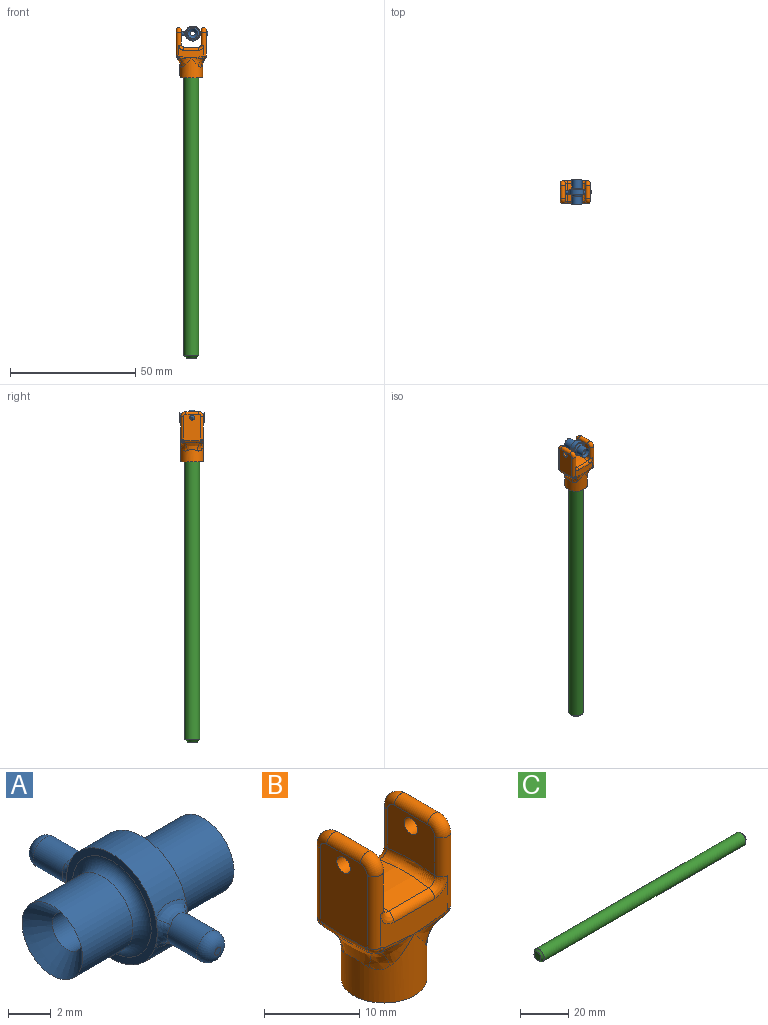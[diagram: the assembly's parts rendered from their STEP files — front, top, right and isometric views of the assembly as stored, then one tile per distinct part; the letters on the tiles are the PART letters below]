
ASSEMBLY  parts=3 mates=1
PART A: 27 faces, bbox 10.1x12.1x6.6 mm
  f0: cylinder r=3mm len=5.74mm, axis (1,0,0), area 14.3mm2, adj f4,f5,f14,f18
  f1: cylinder r=1mm len=2.93mm, axis (1,0,0), area 18.4mm2, adj f8,f25
  f2: cylinder r=3mm len=5.81mm, axis (1,0,0), area 14.8mm2, adj f4,f5,f15,f19
  f3: cylinder r=2mm len=4mm, axis (1,0,0), area 43.6mm2, adj f7,f23
  f4: plane 6.08x6.08mm, normal (1,0,0), area 7mm2, adj f0,f2,f16,f17,f23
  f5: plane 6.08x6.08mm, normal (-1,0,0), area 7mm2, adj f0,f2,f13,f20,f24
  f6: cylinder r=2mm len=4mm, axis (1,0,0), area 41.9mm2, adj f8,f24
  f7: cone r=1mm half-angle=45deg, axis (1,0,0), area 13.1mm2, adj f3,f26
  f8: cone r=2mm half-angle=45deg, axis (-1,0,0), area 13.3mm2, adj f1,f6
  f9: plane 0.4x0.4mm, normal (0,1,0), area 0.1mm2, adj f21
  f10: cylinder r=0.8mm len=2.11mm, axis (0,1,0), area 10mm2, adj f17,f18,f19,f20,f21
  f11: plane 0.4x0.4mm, normal (0,-1,0), area 0.1mm2, adj f22
  f12: cylinder r=0.8mm len=2.11mm, axis (0,1,0), area 10mm2, adj f13,f14,f15,f16,f22
  f13: bspline ~1.77x0.65mm, area 0.8mm2, adj f5,f12,f14,f15
  f14: bspline ~2.33x0.81mm, area 1.2mm2, adj f0,f12,f13,f16
  f15: bspline ~2x0.7mm, area 1.3mm2, adj f2,f12,f13,f16
  f16: bspline ~1.78x0.67mm, area 0.8mm2, adj f4,f12,f14,f15
  f17: bspline ~1.77x0.65mm, area 0.8mm2, adj f4,f10,f18,f19
  f18: bspline ~2.33x0.81mm, area 1.2mm2, adj f0,f10,f17,f20
  f19: bspline ~2x0.7mm, area 1.3mm2, adj f2,f10,f17,f20
  f20: bspline ~1.78x0.67mm, area 0.8mm2, adj f5,f10,f18,f19
  f21: torus R=0.2mm, axis (0,-1,0), area 3.4mm2, adj f9,f10
  f22: torus R=0.2mm, axis (0,-1,0), area 3.4mm2, adj f11,f12
  f23: torus R=2.6mm, axis (1,0,0), area 13.1mm2, adj f3,f4
  f24: torus R=2.6mm, axis (1,0,0), area 13.1mm2, adj f5,f6
  f25: plane 2.04x2.04mm, normal (1,0,0), area 0.1mm2, adj f1,f26
  f26: cylinder r=1.02mm len=5.09mm, axis (-1,0,0), area 32.7mm2, adj f7,f25
PART B: 63 faces, bbox 12.4x9.7x20.5 mm
  f0: plane 10.37x5.36mm, normal (0,1,0), area 29.1mm2, adj f12,f14,f38,f39,f40,f41,f42,f43
  f1: plane 10.33x5.33mm, normal (0,-1,0), area 29.1mm2, adj f8,f13,f30,f31,f32,f49,f50,f51
  f2: plane 7x6mm, normal (-1,0,0), area 37.2mm2, adj f8,f9,f10,f11,f12,f28,f54
  f3: cylinder r=4.5mm len=9mm, axis (0,0,-1), area 148.7mm2, adj f18,f19,f20,f21,f22,f23,f24,f25
  f4: plane 7x6mm, normal (1,0,0), area 37.2mm2, adj f13,f14,f15,f16,f17,f29,f57
  f5: plane 10.55x7mm, normal (-1,0,0), area 69.9mm2, adj f13,f14,f15,f16,f17,f29,f34,f35
  f6: plane 10.55x7mm, normal (1,0,0), area 69.9mm2, adj f8,f9,f10,f11,f12,f28,f45,f46
  f7: cylinder r=21.21mm len=7.35mm, axis (-1,0,0), area 44.3mm2, adj f53,f54,f57,f58
  f8: cylinder r=1mm len=9.36mm, axis (0,0,1), area 22.6mm2, adj f1,f2,f6,f9,f48,f56
  f9: torus R=1mm, axis (-1,0,0), area 8.1mm2, adj f2,f6,f8,f10
  f10: cylinder r=1mm len=5mm, axis (0,-1,0), area 15.7mm2, adj f2,f6,f9,f11
  f11: torus R=1mm, axis (-1,0,0), area 8.1mm2, adj f2,f6,f10,f12
  f12: cylinder r=1mm len=9.36mm, axis (0,0,-1), area 22.6mm2, adj f0,f2,f6,f11,f44,f52
  f13: cylinder r=1mm len=9.36mm, axis (0,0,-1), area 22.6mm2, adj f1,f4,f5,f15,f33,f59
  f14: cylinder r=1mm len=9.36mm, axis (0,0,1), area 22.6mm2, adj f0,f4,f5,f16,f37,f55
  f15: torus R=1mm, axis (-1,0,0), area 8.1mm2, adj f4,f5,f13,f17
  f16: torus R=1mm, axis (-1,0,0), area 8.1mm2, adj f4,f5,f14,f17
  f17: cylinder r=1mm len=5mm, axis (0,1,0), area 15.7mm2, adj f4,f5,f15,f16
  f18: bspline ~5.51x3.49mm, area 4.6mm2, adj f3,f19,f41
  f19: bspline ~3.75x3.7mm, area 6.7mm2, adj f3,f18,f20,f42,f43,f45
  f20: bspline ~8.76x3.84mm, area 17mm2, adj f3,f19,f21,f46
  f21: bspline ~3.75x3.6mm, area 6.7mm2, adj f3,f20,f22,f47,f49,f50
  f22: bspline ~5.51x3.49mm, area 4.6mm2, adj f3,f21,f51
  f23: bspline ~5.51x3.49mm, area 4.6mm2, adj f3,f24,f30
  f24: bspline ~3.75x3.7mm, area 6.7mm2, adj f3,f23,f25,f31,f32,f34
  f25: bspline ~8.76x3.84mm, area 17mm2, adj f3,f24,f26,f35
  f26: bspline ~3.75x3.6mm, area 6.7mm2, adj f3,f25,f27,f36,f38,f39
  f27: bspline ~5.51x3.49mm, area 4.6mm2, adj f3,f26,f40
  f28: cylinder r=1mm len=2mm, axis (1,0,0), area 12.6mm2, adj f2,f6
  f29: cylinder r=1mm len=2mm, axis (1,0,0), area 12.6mm2, adj f4,f5
  f30: bspline ~4.78x0.76mm, area 1.2mm2, adj f1,f23,f31
  f31: bspline ~0.8x0.45mm, area 0.1mm2, adj f1,f24,f30,f32
  f32: bspline ~1.15x1.11mm, area 0.7mm2, adj f1,f24,f31,f33
  f33: sphere r=1mm, area 1.1mm2, adj f13,f32,f34
  f34: bspline ~0.98x0.87mm, area 0.5mm2, adj f5,f24,f33,f35
  f35: bspline ~6.85x0.85mm, area 5.5mm2, adj f5,f25,f34,f36
  f36: bspline ~0.97x0.85mm, area 0.5mm2, adj f5,f26,f35,f37
  f37: sphere r=1mm, area 1.1mm2, adj f14,f36,f38
  f38: bspline ~1.2x1.14mm, area 0.7mm2, adj f0,f26,f37,f39
  f39: bspline ~0.79x0.44mm, area 0.1mm2, adj f0,f26,f38,f40
  f40: bspline ~4.9x0.78mm, area 1.2mm2, adj f0,f27,f39
  f41: bspline ~4.69x0.74mm, area 1.2mm2, adj f0,f18,f42
  f42: bspline ~0.8x0.45mm, area 0.1mm2, adj f0,f19,f41,f43
  f43: bspline ~1.31x1.18mm, area 0.7mm2, adj f0,f19,f42,f44
  f44: sphere r=1mm, area 1mm2, adj f12,f43,f45
  f45: bspline ~0.98x0.85mm, area 0.5mm2, adj f6,f19,f44,f46
  f46: bspline ~7.61x0.93mm, area 5.5mm2, adj f6,f20,f45,f47
  f47: bspline ~0.98x0.85mm, area 0.5mm2, adj f6,f21,f46,f48
  f48: sphere r=1mm, area 1mm2, adj f8,f47,f49
  f49: bspline ~1.2x1.14mm, area 0.7mm2, adj f1,f21,f48,f50
  f50: bspline ~0.8x0.44mm, area 0.1mm2, adj f1,f21,f49,f51
  f51: bspline ~4.69x0.74mm, area 1.2mm2, adj f1,f22,f50
  f52: bspline ~2.44x2.36mm, area 3.2mm2, adj f0,f12,f53,f54
  f53: cylinder r=1mm len=6mm, axis (-1,0,0), area 8.4mm2, adj f0,f7,f52,f55
  f54: torus R=22.21mm, axis (-1,0,0), area 11.3mm2, adj f2,f7,f52,f56
  f55: bspline ~2.49x2.36mm, area 3.2mm2, adj f0,f14,f53,f57
  f56: bspline ~2.49x2.36mm, area 3.2mm2, adj f1,f8,f54,f58
  f57: torus R=22.21mm, axis (-1,0,0), area 11.3mm2, adj f4,f7,f55,f59
  f58: cylinder r=1mm len=6mm, axis (-1,0,0), area 8.4mm2, adj f1,f7,f56,f59
  f59: bspline ~2.44x2.36mm, area 3.2mm2, adj f1,f13,f57,f58
  f60: plane 9x9mm, normal (0,0,-1), area 32.9mm2, adj f3,f62
  f61: plane 6.25x6.25mm, normal (0,0,-1), area 30.7mm2, adj f62
  f62: cylinder r=3.12mm len=8mm, axis (0,0,-1), area 157.1mm2, adj f60,f61
PART C: 5 faces, bbox 120x6x6 mm
  f0: cylinder r=3mm len=118mm, axis (-1,0,0), area 2224.2mm2, adj f3,f4
  f1: plane 4x4mm, normal (1,0,0), area 12.6mm2, adj f4
  f2: plane 4x4mm, normal (-1,0,0), area 12.6mm2, adj f3
  f3: cone r=3mm half-angle=45deg, axis (1,0,0), area 22.2mm2, adj f0,f2
  f4: cone r=2mm half-angle=45deg, axis (-1,0,0), area 22.2mm2, adj f0,f1
PLACE A rot(axis=(0,0,1),90deg) t=(24.9,154.65,37.51)mm
PLACE B t=(93.04,135.26,78.79)mm
PLACE C rot(axis=(0,1,0),90deg) t=(-50.3,-8.36,22.79)mm
MATE revolute A.f10 <-> B.f28  axis (1,0,0) through (30.3,70.69,92.35)mm
